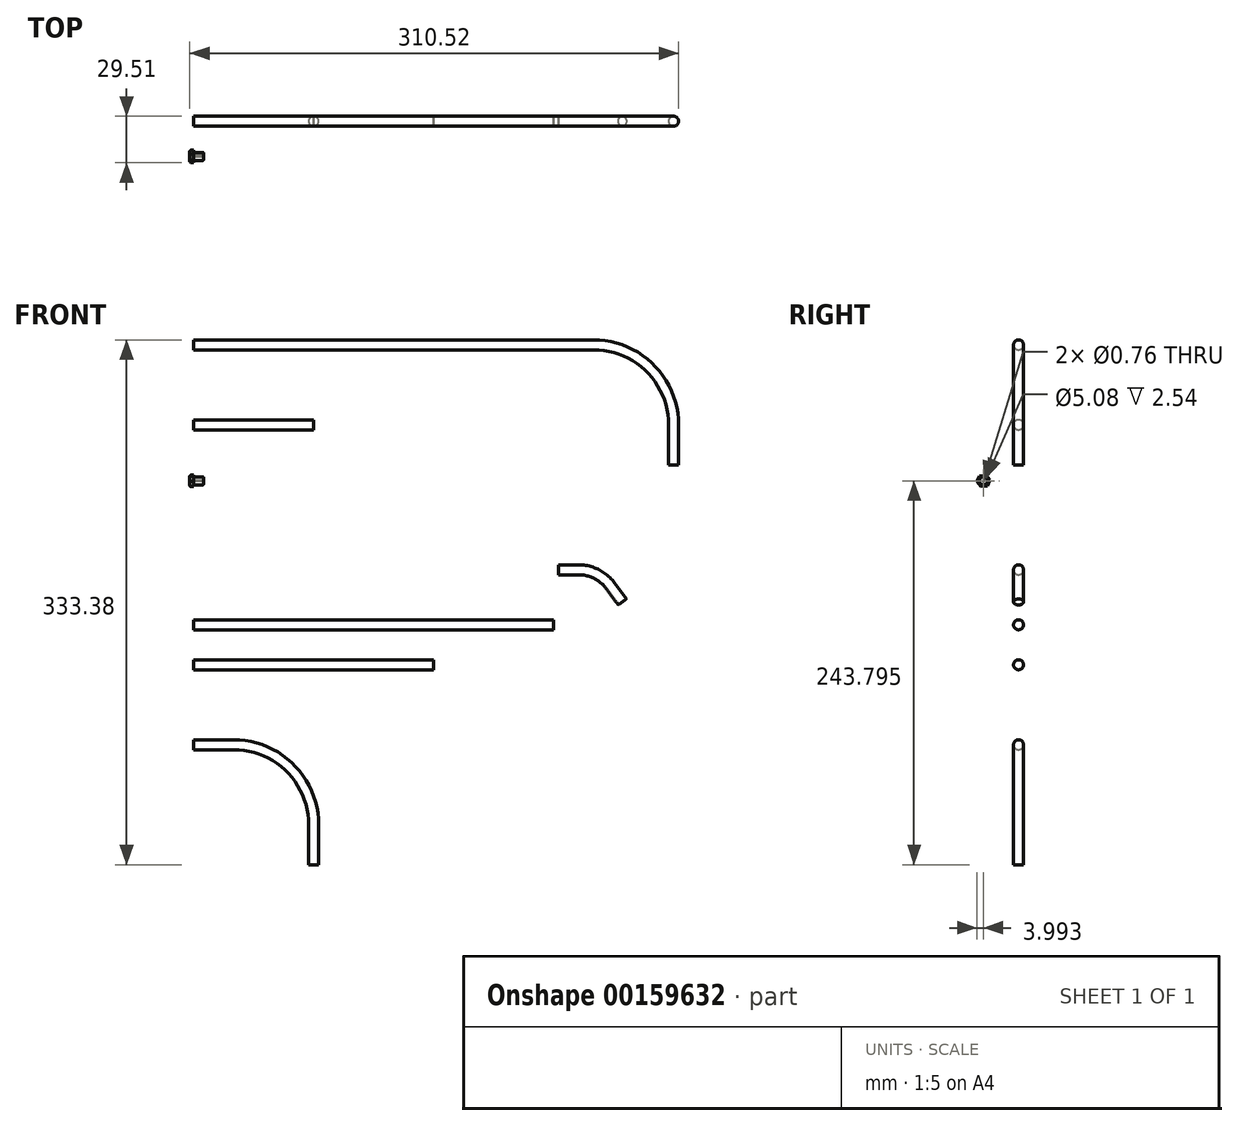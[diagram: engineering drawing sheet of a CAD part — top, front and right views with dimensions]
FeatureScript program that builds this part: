
annotation { "Feature Type Name" : "Feature", "Feature Type Description" : "" }
export const myFeature = defineFeature(function(context is Context, id is Id, definition is map)
    precondition{}
    {
        {
            var Q0;
            Q0=qCreatedBy(makeId("Front.planeOp"),FACE);
            var sketch = newSketch(context, id + "F0", { "sketchPlane" : qUnion([Q0])});
            skLineSegment(sketch, "E0", {"start": v(0, 0) * mm, "end": v(254, 0) * mm});
            skLineSegment(sketch, "E1", {"start": v(304.8, -50.8) * mm, "end": v(304.8, -76.2) * mm});
            skPoint(sketch, "E2.visualSharp", {"position": v(304.8, 0) * mm});
            skArc(sketch, "E2.filletArc", {"start": v(304.8, -50.8) * mm, "mid": v(289.92, -14.88) * mm, "end": v(254, 0) * mm});
            skSolve(sketch);
        }
        {
            var Q0;
            Q0=qCreatedBy(makeId("Right.planeOp"),FACE);
            var sketch = newSketch(context, id + "F1", { "sketchPlane" : qUnion([Q0])});
            skCircle(sketch, "E3", {"center": v(0, 0) * mm, "radius": 3.18 * mm});
            skSolve(sketch);
        }
        {
            var Q0;
            Q0=makeQuery(id+"F1.imprint","IMPRINT",FACE,{"disambiguationData":[TD([[makeQuery(id+"F1.imprint","IMPRINT",EDGE,{"derivedFrom":sQuery(id+"F1.wireOp",EDGE,"E3")}),1.0]])]});
            var Q1;
            Q1=sQuery(id+"F0.wireOp",EDGE,"E0");
            var Q2;
            Q2=sQuery(id+"F0.wireOp",EDGE,"E2.filletArc");
            var Q3;
            Q3=sQuery(id+"F0.wireOp",EDGE,"E1");
            sweep(context, id + "F2", {"profiles" : qUnion([Q0]), "path" : qUnion([Q1, Q2, Q3])});
        }
        {
            var Q0;
            Q0=makeQuery(id+"F2.opSweep","SWEPT_BODY",BODY,{"disambiguationData":[OSD([sQuery(id+"F0.wireOp",EDGE,"E1"),sQuery(id+"F1.wireOp",EDGE,"E3")])]});
            transform(context, id + "F3", {"entities" : qUnion([Q0]), "transformType" : TransformType.TRANSLATION_3D, "dx" : 0 * mm, "dy" : 0 * mm, "dz" : 127 * mm, "makeCopy" : false});
        }
        {
            var Q0;
            Q0=qCreatedBy(makeId("Front.planeOp"),FACE);
            var sketch = newSketch(context, id + "F4", { "sketchPlane" : qUnion([Q0])});
            skLineSegment(sketch, "E4", {"start": v(0, 0) * mm, "end": v(25.4, 0) * mm});
            skLineSegment(sketch, "E5", {"start": v(76.2, -50.8) * mm, "end": v(76.2, -76.2) * mm});
            skPoint(sketch, "E6.visualSharp", {"position": v(76.2, 0) * mm});
            skArc(sketch, "E6.filletArc", {"start": v(76.2, -50.8) * mm, "mid": v(61.32, -14.88) * mm, "end": v(25.4, 0) * mm});
            skSolve(sketch);
        }
        {
            var Q0;
            Q0=qCreatedBy(makeId("Right.planeOp"),FACE);
            var sketch = newSketch(context, id + "F5", { "sketchPlane" : qUnion([Q0])});
            skCircle(sketch, "E7", {"center": v(0, 0) * mm, "radius": 3.18 * mm});
            skSolve(sketch);
        }
        {
            var Q0;
            Q0=makeQuery(id+"F5.imprint","IMPRINT",FACE,{"disambiguationData":[TD([[makeQuery(id+"F5.imprint","IMPRINT",EDGE,{"derivedFrom":sQuery(id+"F5.wireOp",EDGE,"E7")}),1.0]])]});
            var Q1;
            Q1=sQuery(id+"F4.wireOp",EDGE,"E6.filletArc");
            var Q2;
            Q2=sQuery(id+"F4.wireOp",EDGE,"E5");
            var Q3;
            Q3=sQuery(id+"F4.wireOp",EDGE,"E4");
            sweep(context, id + "F6", {"profiles" : qUnion([Q0]), "path" : qUnion([Q1, Q2, Q3])});
        }
        {
            var Q0;
            Q0=makeQuery(id+"F6.opSweep","SWEPT_BODY",BODY,{"disambiguationData":[OSD([sQuery(id+"F4.wireOp",EDGE,"E5"),sQuery(id+"F5.wireOp",EDGE,"E7")])]});
            transform(context, id + "F7", {"entities" : qUnion([Q0]), "transformType" : TransformType.TRANSLATION_3D, "dx" : 0 * mm, "dy" : 0 * mm, "dz" : -127 * mm, "makeCopy" : false});
        }
        {
            var Q0;
            Q0=qCreatedBy(makeId("Front.planeOp"),FACE);
            var sketch = newSketch(context, id + "F8", { "sketchPlane" : qUnion([Q0])});
            skLineSegment(sketch, "E8", {"start": v(0, 0) * mm, "end": v(152.4, 0) * mm});
            skSolve(sketch);
        }
        {
            var Q0;
            Q0=makeQuery(id+"F5.imprint","IMPRINT",FACE,{"disambiguationData":[TD([[makeQuery(id+"F5.imprint","IMPRINT",EDGE,{"derivedFrom":sQuery(id+"F5.wireOp",EDGE,"E7")}),1.0]])]});
            var Q1;
            Q1=sQuery(id+"F8.wireOp",EDGE,"E8");
            sweep(context, id + "F9", {"profiles" : qUnion([Q0]), "path" : qUnion([Q1])});
        }
        {
            var Q0;
            Q0=makeQuery(id+"F9.opSweep","SWEPT_BODY",BODY,{"disambiguationData":[OSD([sQuery(id+"F5.wireOp",EDGE,"E7"),sQuery(id+"F8.wireOp",EDGE,"E8")])]});
            transform(context, id + "F10", {"entities" : qUnion([Q0]), "transformType" : TransformType.TRANSLATION_3D, "dx" : 0 * mm, "dy" : 0 * mm, "dz" : -76.2 * mm, "makeCopy" : false});
        }
        {
            var Q0;
            Q0=qCreatedBy(makeId("Front.planeOp"),FACE);
            var sketch = newSketch(context, id + "F11", { "sketchPlane" : qUnion([Q0])});
            skLineSegment(sketch, "E9", {"start": v(0, 0) * mm, "end": v(76.2, 0) * mm});
            skSolve(sketch);
        }
        {
            var Q0;
            Q0=makeQuery(id+"F5.imprint","IMPRINT",FACE,{"disambiguationData":[TD([[makeQuery(id+"F5.imprint","IMPRINT",EDGE,{"derivedFrom":sQuery(id+"F5.wireOp",EDGE,"E7")}),1.0]])]});
            var Q1;
            Q1=sQuery(id+"F11.wireOp",EDGE,"E9");
            sweep(context, id + "F12", {"profiles" : qUnion([Q0]), "path" : qUnion([Q1])});
        }
        {
            var Q0;
            Q0=makeQuery(id+"F12.opSweep","SWEPT_BODY",BODY,{"disambiguationData":[OSD([sQuery(id+"F5.wireOp",EDGE,"E7"),sQuery(id+"F11.wireOp",EDGE,"E9")])]});
            transform(context, id + "F13", {"entities" : qUnion([Q0]), "transformType" : TransformType.TRANSLATION_3D, "dx" : 0 * mm, "dy" : 0 * mm, "dz" : 76.2 * mm, "makeCopy" : false});
        }
        {
            var Q0;
            Q0=qCreatedBy(makeId("Front.planeOp"),FACE);
            var sketch = newSketch(context, id + "F14", { "sketchPlane" : qUnion([Q0])});
            skLineSegment(sketch, "E10", {"start": v(0, 0) * mm, "end": v(228.6, 0) * mm});
            skSolve(sketch);
        }
        {
            var Q0;
            Q0=makeQuery(id+"F5.imprint","IMPRINT",FACE,{"disambiguationData":[TD([[makeQuery(id+"F5.imprint","IMPRINT",EDGE,{"derivedFrom":sQuery(id+"F5.wireOp",EDGE,"E7")}),1.0]])]});
            var Q1;
            Q1=sQuery(id+"F14.wireOp",EDGE,"E10");
            sweep(context, id + "F15", {"profiles" : qUnion([Q0]), "path" : qUnion([Q1])});
        }
        {
            var Q0;
            Q0=makeQuery(id+"F15.opSweep","SWEPT_BODY",BODY,{"disambiguationData":[OSD([sQuery(id+"F5.wireOp",EDGE,"E7"),sQuery(id+"F14.wireOp",EDGE,"E10")])]});
            transform(context, id + "F16", {"entities" : qUnion([Q0]), "transformType" : TransformType.TRANSLATION_3D, "dx" : 0 * mm, "dy" : 0 * mm, "dz" : -50.8 * mm, "makeCopy" : false});
        }
        {
            var Q0;
            Q0=qCreatedBy(makeId("Front.planeOp"),FACE);
            var sketch = newSketch(context, id + "F17", { "sketchPlane" : qUnion([Q0])});
            skLineSegment(sketch, "E11", {"start": v(0, 0) * mm, "end": v(12.56, 0) * mm});
            skLineSegment(sketch, "E12", {"start": v(33.01, -10.34) * mm, "end": v(40.46, -20.45) * mm});
            skPoint(sketch, "E13.visualSharp", {"position": v(25.4, 0) * mm});
            skArc(sketch, "E13.filletArc", {"start": v(33.01, -10.34) * mm, "mid": v(24.02, -2.73) * mm, "end": v(12.56, 0) * mm});
            skSolve(sketch);
        }
        {
            var Q0;
            Q0=makeQuery(id+"F5.imprint","IMPRINT",FACE,{"disambiguationData":[TD([[makeQuery(id+"F5.imprint","IMPRINT",EDGE,{"derivedFrom":sQuery(id+"F5.wireOp",EDGE,"E7")}),1.0]])]});
            var Q1;
            Q1=sQuery(id+"F17.wireOp",EDGE,"E11");
            var Q2;
            Q2=sQuery(id+"F17.wireOp",EDGE,"E13.filletArc");
            var Q3;
            Q3=sQuery(id+"F17.wireOp",EDGE,"E12");
            sweep(context, id + "F18", {"profiles" : qUnion([Q0]), "path" : qUnion([Q1, Q2, Q3])});
        }
        {
            var Q0;
            Q0=makeQuery(id+"F18.opSweep","SWEPT_BODY",BODY,{"disambiguationData":[OSD([sQuery(id+"F5.wireOp",EDGE,"E7"),sQuery(id+"F17.wireOp",EDGE,"E12")])]});
            transform(context, id + "F19", {"entities" : qUnion([Q0]), "transformType" : TransformType.TRANSLATION_3D, "dx" : 231.77 * mm, "dy" : 0 * mm, "dz" : -15.88 * mm, "makeCopy" : false});
        }
        {
            var Q0;
            Q0=qCreatedBy(makeId("Right.planeOp"),FACE);
            var sketch = newSketch(context, id + "F20", { "sketchPlane" : qUnion([Q0])});
            skCircle(sketch, "E14.cCircle", {"center": v(-22.34, 40.6) * mm, "radius": 5.56 * mm, "construction": true});
            skLineSegment(sketch, "E14.0", {"start": v(-23.88, 36.87) * mm, "end": v(-26.33, 40.06) * mm});
            skLineSegment(sketch, "E14.1", {"start": v(-26.33, 40.06) * mm, "end": v(-24.8, 43.8) * mm});
            skLineSegment(sketch, "E14.2", {"start": v(-24.8, 43.8) * mm, "end": v(-20.8, 44.32) * mm});
            skLineSegment(sketch, "E14.3", {"start": v(-20.8, 44.32) * mm, "end": v(-18.34, 41.13) * mm});
            skLineSegment(sketch, "E14.4", {"start": v(-18.34, 41.13) * mm, "end": v(-19.88, 37.4) * mm});
            skLineSegment(sketch, "E14.5", {"start": v(-19.88, 37.4) * mm, "end": v(-23.88, 36.87) * mm});
            skPoint(sketch, "E14.0.midPoint", {"position": v(-25.1, 38.47) * mm});
            skCircle(sketch, "E15", {"center": v(-22.34, 40.6) * mm, "radius": 2.54 * mm});
            skSolve(sketch);
        }
        {
            var Q0;
            Q0=makeQuery(id+"F20.imprint","IMPRINT",FACE,{"disambiguationData":[TD([[makeQuery(id+"F20.imprint","IMPRINT",EDGE,{"derivedFrom":sQuery(id+"F20.wireOp",EDGE,"E15")}),1.0]])]});
            extrude(context, id + "F21", {"entities" : qUnion([Q0]), "depth" : 6.35 * mm});
        }
        {
            var Q0;
            Q0=makeQuery(id+"F20.imprint","IMPRINT",FACE,{"disambiguationData":[TD([[makeQuery(id+"F20.imprint","IMPRINT",EDGE,{"derivedFrom":sQuery(id+"F20.wireOp",EDGE,"E14.0")}),-1.0]])]});
            extrude(context, id + "F22", {"entities" : qUnion([Q0]), "oppositeDirection" : true, "depth" : 2.54 * mm});
        }
        {
            var Q0;
            Q0=makeQuery(id+"F21.opExtrude","CAP_EDGE",EDGE,{"disambiguationData":[OSD([sQuery(id+"F20.wireOp",EDGE,"E15")])],"isStart":false});
            fillet(context, id + "F23", {"entities" : qUnion([Q0]), "radius" : 0.76 * mm, "tangentPropagation" : true, "allowEdgeOverflow" : false});
        }
        {
            var Q0;
            Q0=makeQuery(id+"F21.opExtrude","CAP_FACE",FACE,{"disambiguationData":[OSD([sQuery(id+"F20.wireOp",EDGE,"E15")])],"isStart":true});
            extrude(context, id + "F24", {"entities" : qUnion([Q0]), "depth" : 2.54 * mm});
        }
        {
            var Q0;
            Q0=makeQuery(id+"F22.opExtrude","CAP_EDGE",EDGE,{"disambiguationData":[OSD([sQuery(id+"F20.wireOp",EDGE,"E14.0")])],"isStart":false});
            var Q1;
            Q1=makeQuery(id+"F22.opExtrude","CAP_EDGE",EDGE,{"disambiguationData":[OSD([sQuery(id+"F20.wireOp",EDGE,"E14.2")])],"isStart":false});
            var Q2;
            Q2=makeQuery(id+"F22.opExtrude","CAP_EDGE",EDGE,{"disambiguationData":[OSD([sQuery(id+"F20.wireOp",EDGE,"E14.1")])],"isStart":false});
            var Q3;
            Q3=makeQuery(id+"F22.opExtrude","CAP_EDGE",EDGE,{"disambiguationData":[OSD([sQuery(id+"F20.wireOp",EDGE,"E14.3")])],"isStart":false});
            var Q4;
            Q4=makeQuery(id+"F22.opExtrude","CAP_EDGE",EDGE,{"disambiguationData":[OSD([sQuery(id+"F20.wireOp",EDGE,"E14.4")])],"isStart":false});
            var Q5;
            Q5=makeQuery(id+"F22.opExtrude","CAP_EDGE",EDGE,{"disambiguationData":[OSD([sQuery(id+"F20.wireOp",EDGE,"E14.5")])],"isStart":false});
            fillet(context, id + "F25", {"entities" : qUnion([Q0, Q1, Q2, Q3, Q4, Q5]), "radius" : 1.02 * mm, "allowEdgeOverflow" : false});
        }
        {
            var Q0;
            Q0=sQuery(id+"F20.wireOp",VERTEX,"E14.cCircle.center");
            var Q1;
            Q1=makeQuery(id+"F24.opExtrude","SWEPT_BODY",BODY,{"disambiguationData":[OSD([sQuery(id+"F20.wireOp",EDGE,"E15")])]});
            hole(context, id + "F26", {"style" : HoleStyle.SIMPLE, "endStyle" : HoleEndStyle.THROUGH, "holeDiameter" : 0.76 * mm, "locations" : qUnion([Q0]), "scope" : qUnion([Q1]), "isTappedThrough" : true});
        }
        {
            var Q0;
            Q0=sQuery(id+"F20.wireOp",VERTEX,"E14.cCircle.center");
            var Q1;
            Q1=makeQuery(id+"F21.opExtrude","SWEPT_BODY",BODY,{"disambiguationData":[OSD([sQuery(id+"F20.wireOp",EDGE,"E15")])]});
            hole(context, id + "F27", {"style" : HoleStyle.SIMPLE, "endStyle" : HoleEndStyle.THROUGH, "oppositeDirection" : true, "holeDiameter" : 0.76 * mm, "locations" : qUnion([Q0]), "scope" : qUnion([Q1]), "isTappedThrough" : true});
        }
    });
